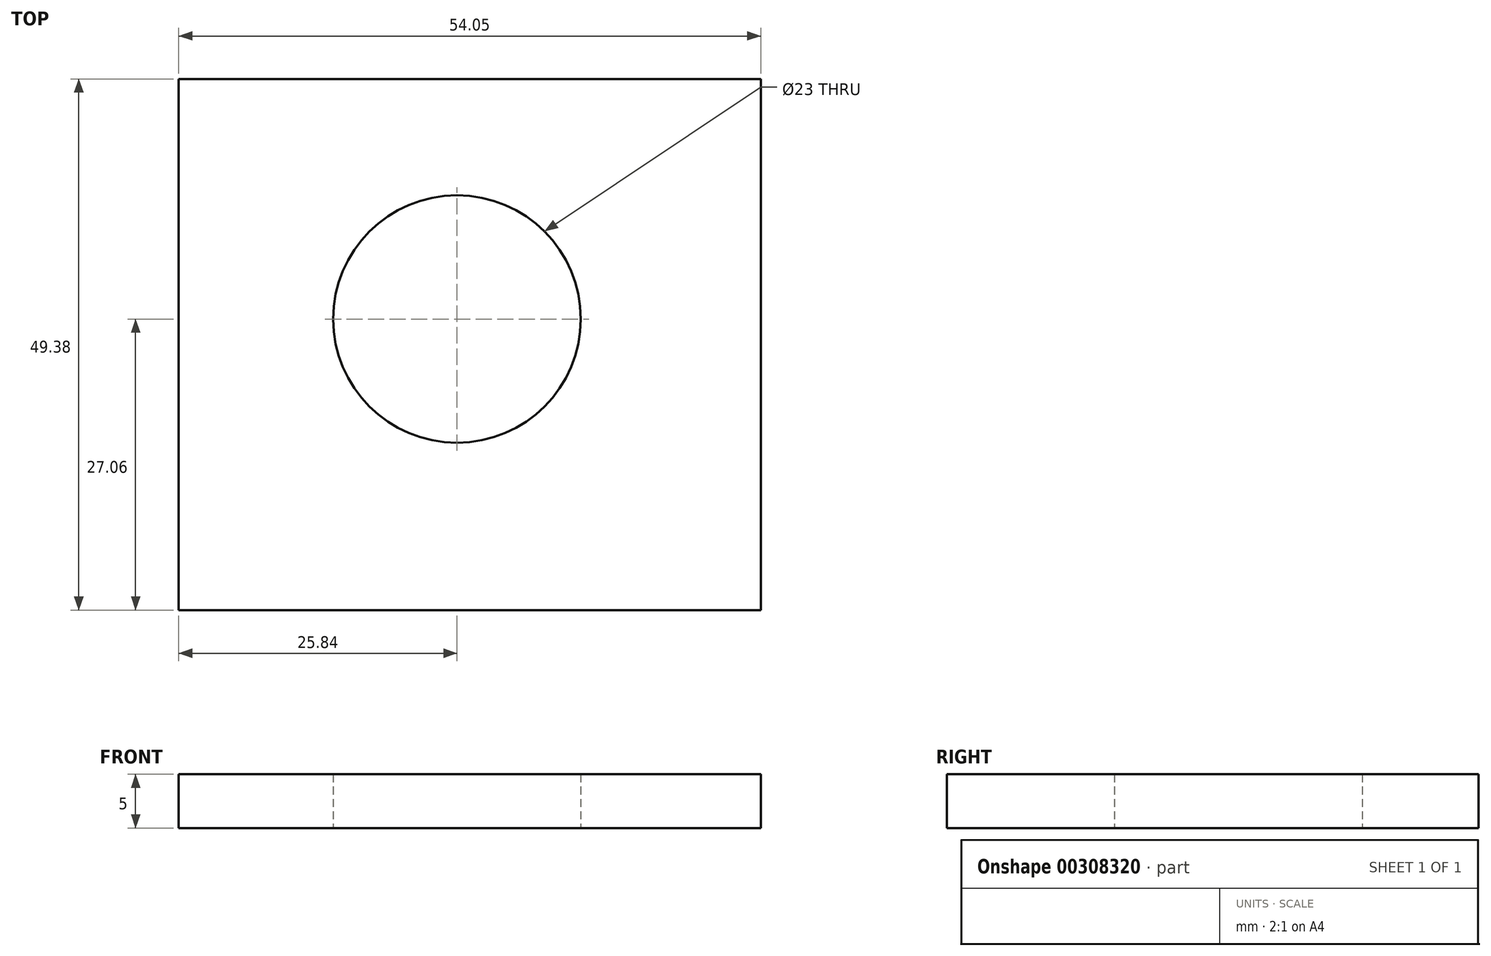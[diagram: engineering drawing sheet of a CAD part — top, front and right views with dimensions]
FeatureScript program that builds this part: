
annotation { "Feature Type Name" : "Feature", "Feature Type Description" : "" }
export const myFeature = defineFeature(function(context is Context, id is Id, definition is map)
    precondition{}
    {
        {
            var Q0;
            Q0=qCreatedBy(makeId("Top.planeOp"),FACE);
            var sketch = newSketch(context, id + "F0", { "sketchPlane" : qUnion([Q0])});
            skLineSegment(sketch, "E0.bottom", {"start": v(-25.84, 22.32) * mm, "end": v(28.21, 22.32) * mm});
            skLineSegment(sketch, "E0.top", {"start": v(-25.84, -27.06) * mm, "end": v(28.21, -27.06) * mm});
            skLineSegment(sketch, "E0.left", {"start": v(-25.84, 22.32) * mm, "end": v(-25.84, -27.06) * mm});
            skLineSegment(sketch, "E0.right", {"start": v(28.21, 22.32) * mm, "end": v(28.21, -27.06) * mm});
            skCircle(sketch, "E1", {"center": v(0, 0) * mm, "radius": 11.5 * mm});
            skSolve(sketch);
        }
        {
            var Q0;
            Q0=makeQuery(id+"F0.imprint","IMPRINT",FACE,{"disambiguationData":[TD([[makeQuery(id+"F0.imprint","IMPRINT",EDGE,{"derivedFrom":sQuery(id+"F0.wireOp",EDGE,"E0.bottom")}),-1.0]])]});
            extrude(context, id + "F1", {"entities" : qUnion([Q0]), "depth" : 5 * mm});
        }
    });
